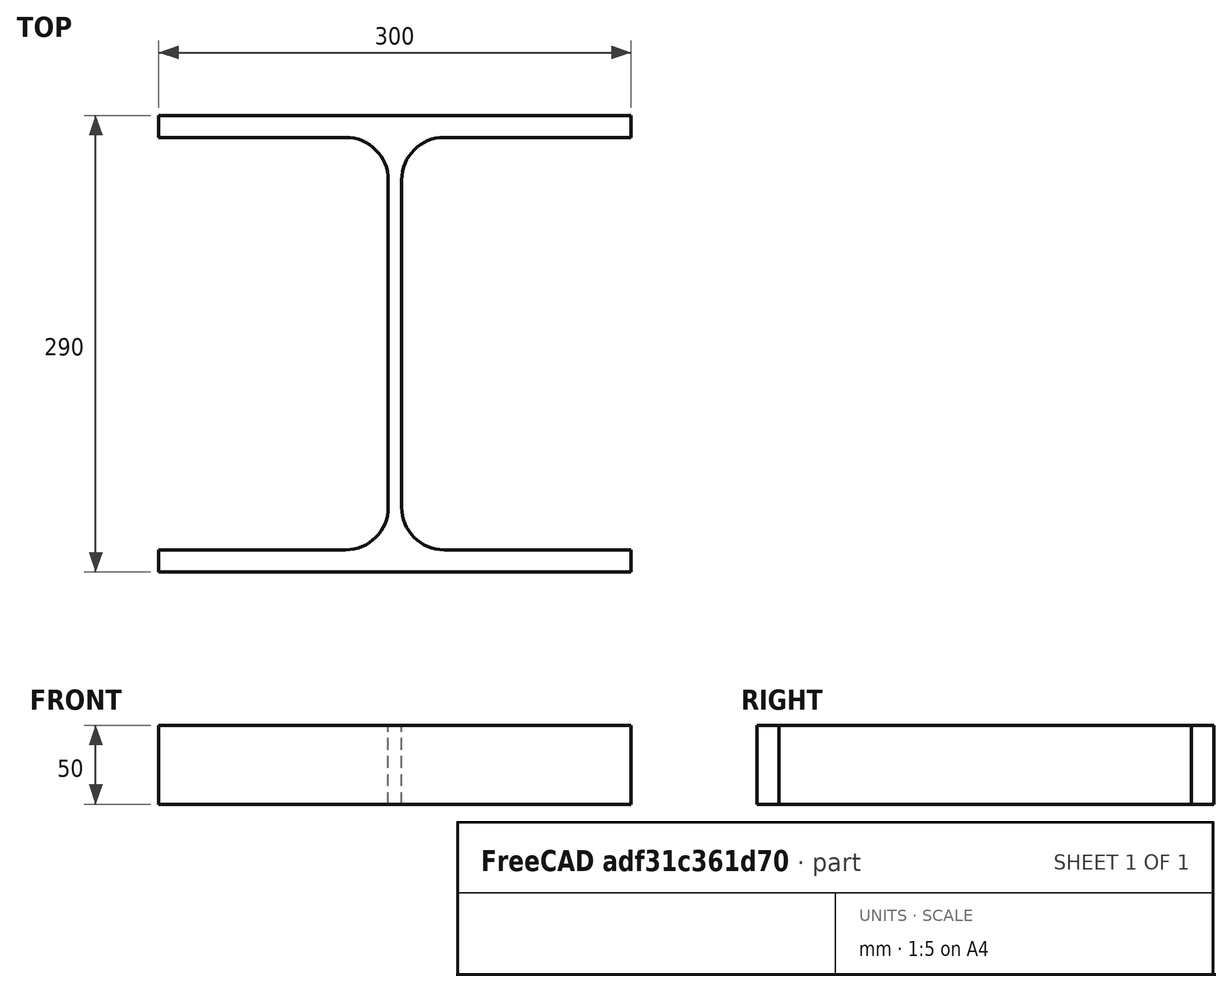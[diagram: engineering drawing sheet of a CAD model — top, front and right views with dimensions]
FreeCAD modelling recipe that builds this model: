
FCSTD DOCUMENT  (FreeCAD 0.15R4671 (Git))
Label: HE-A-Profile 300 DIN1025-3 S235JR
License: All rights reserved
LicenseURL: http://en.wikipedia.org/wiki/All_rights_reserved
objects: Sketcher::SketchObject×1, Part::Extrusion×1
note: 2 computed .brp shape members not serialized (recipe doc carries the construction recipe); baked Part::Feature solids carry a one-line shape summary decoded from their .brp

FEATURE [Sketcher::SketchObject] Sketch
  sketch-geometry (16):
    g0: LineSegment StartX=4.25 StartY=-104 StartZ=0 EndX=4.25 EndY=104 EndZ=0
    g1: LineSegment StartX=31.25 StartY=131 StartZ=0 EndX=150 EndY=131 EndZ=0
    g2: LineSegment StartX=150 StartY=131 StartZ=0 EndX=150 EndY=145 EndZ=0
    g3: LineSegment StartX=150 StartY=145 StartZ=0 EndX=-150 EndY=145 EndZ=0
    g4: LineSegment StartX=-150 StartY=145 StartZ=0 EndX=-150 EndY=131 EndZ=0
    g5: LineSegment StartX=-150 StartY=131 StartZ=0 EndX=-31.25 EndY=131 EndZ=0
    g6: LineSegment StartX=-4.25 StartY=104 StartZ=0 EndX=-4.25 EndY=-104 EndZ=0
    g7: LineSegment StartX=-31.25 StartY=-131 StartZ=0 EndX=-150 EndY=-131 EndZ=0
    g8: LineSegment StartX=-150 StartY=-131 StartZ=0 EndX=-150 EndY=-145 EndZ=0
    g9: LineSegment StartX=-150 StartY=-145 StartZ=0 EndX=150 EndY=-145 EndZ=0
    g10: LineSegment StartX=150 StartY=-145 StartZ=0 EndX=150 EndY=-131 EndZ=0
    g11: LineSegment StartX=150 StartY=-131 StartZ=0 EndX=31.25 EndY=-131 EndZ=0
    g12: ArcOfCircle CenterX=31.25 CenterY=104 CenterZ=0 NormalX=0 NormalY=0 NormalZ=1 Radius=27 StartAngle=1.5708 EndAngle=3.14159
    g13: ArcOfCircle CenterX=31.25 CenterY=-104 CenterZ=0 NormalX=0 NormalY=0 NormalZ=1 Radius=27 StartAngle=3.14159 EndAngle=4.71239
    g14: ArcOfCircle CenterX=-31.25 CenterY=104 CenterZ=0 NormalX=0 NormalY=0 NormalZ=1 Radius=27 StartAngle=0 EndAngle=1.5708
    g15: ArcOfCircle CenterX=-31.25 CenterY=-104 CenterZ=0 NormalX=0 NormalY=0 NormalZ=1 Radius=27 StartAngle=4.71239 EndAngle=6.28319
  constraints (42):
    c: Vertical(g0)
    c: Coincident(g2,g1)
    c: Vertical(g2)
    c: Coincident(g3,g2)
    c: Coincident(g4,g3)
    c: Vertical(g4)
    c: Coincident(g5,g4)
    c: Horizontal(g5)
    c: Vertical(g6)
    c: Horizontal(g7)
    c: Coincident(g8,g7)
    c: Vertical(g8)
    c: Coincident(g9,g8)
    c: Horizontal(g9)
    c: Coincident(g10,g9)
    c: Vertical(g10)
    c: Coincident(g11,g10)
    c: Horizontal(g11)
    c: Tangent(g1,g12) = 1.5708
    c: Tangent(g0,g12) = 1.5708
    c: Tangent(g0,g13) = 1.5708
    c: Tangent(g11,g13) = 1.5708
    c: Tangent(g5,g14) = 1.5708
    c: Tangent(g6,g14) = 1.5708
    c: Tangent(g6,g15) = 1.5708
    c: Tangent(g7,g15) = 1.5708
    c: Equal(g3,g9)
    c: Equal(g2,g4)
    c: Equal(g4,g8)
    c: Equal(g8,g10)
    c: Equal(g12,g14)
    c: Equal(g14,g15)
    c: Equal(g15,g13)
    c: Symmetric(g2,g3,g-2)
    c: Symmetric(g9,g8,g-2)
    c: Symmetric(g0,g6,g-2)
    c: Symmetric(g2,g9,g-1)
    c: DistanceY(g2,g9) = -290
    c: DistanceX(g3) = -300
    c: DistanceX(g0,g6) = -8.5
    c: DistanceY(g2) = 14
    c: Radius(g12) = 27
FEATURE [Part::Extrusion] Extrude  label="HE-A-Profile 300 DIN1025-3 S235JR"
  Base = -> Sketch
  Dir = (0,0,50)
  Solid = true
